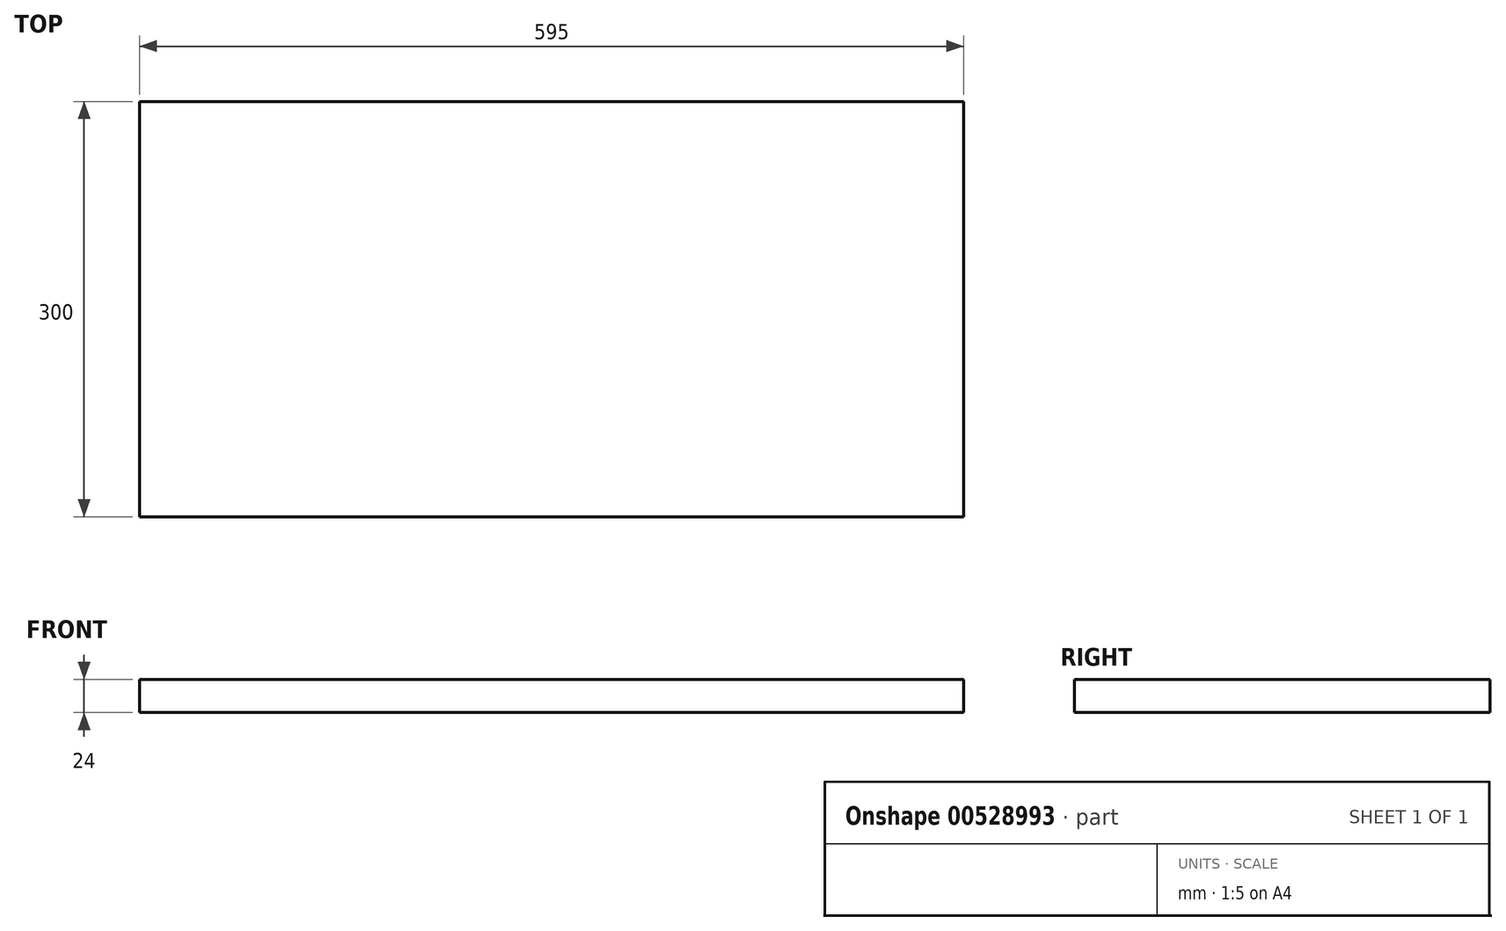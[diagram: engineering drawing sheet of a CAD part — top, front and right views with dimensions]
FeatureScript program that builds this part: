
annotation { "Feature Type Name" : "Feature", "Feature Type Description" : "" }
export const myFeature = defineFeature(function(context is Context, id is Id, definition is map)
    precondition{}
    {
        {
            var Q0;
            Q0=qCreatedBy(makeId("Front.planeOp"),FACE);
            var sketch = newSketch(context, id + "F0", { "sketchPlane" : qUnion([Q0])});
            skLineSegment(sketch, "E0", {"start": v(-58.18, 31.83) * mm, "end": v(-33.18, 31.83) * mm});
            skLineSegment(sketch, "E1", {"start": v(-58.18, 31.83) * mm, "end": v(-346.18, 31.83) * mm});
            skLineSegment(sketch, "E2", {"start": v(-346.18, 31.83) * mm, "end": v(-346.18, 7.83) * mm});
            skLineSegment(sketch, "E3", {"start": v(-346.18, 7.83) * mm, "end": v(-33.18, 7.83) * mm});
            skLineSegment(sketch, "E4", {"start": v(-33.18, 7.83) * mm, "end": v(248.82, 7.83) * mm});
            skLineSegment(sketch, "E5", {"start": v(248.82, 7.83) * mm, "end": v(248.82, 31.83) * mm});
            skLineSegment(sketch, "E6", {"start": v(248.82, 31.83) * mm, "end": v(-33.18, 31.83) * mm});
            skLineSegment(sketch, "E7", {"start": v(-33.18, 31.83) * mm, "end": v(-33.18, 7.83) * mm});
            skLineSegment(sketch, "E8", {"start": v(-58.18, 31.83) * mm, "end": v(-58.18, 7.83) * mm});
            skSolve(sketch);
        }
        {
            var Q0;
            Q0=qSketchRegion(id+"F0",true);
            extrude(context, id + "F1", {"entities" : qUnion([Q0]), "depth" : 300 * mm});
        }
    });
